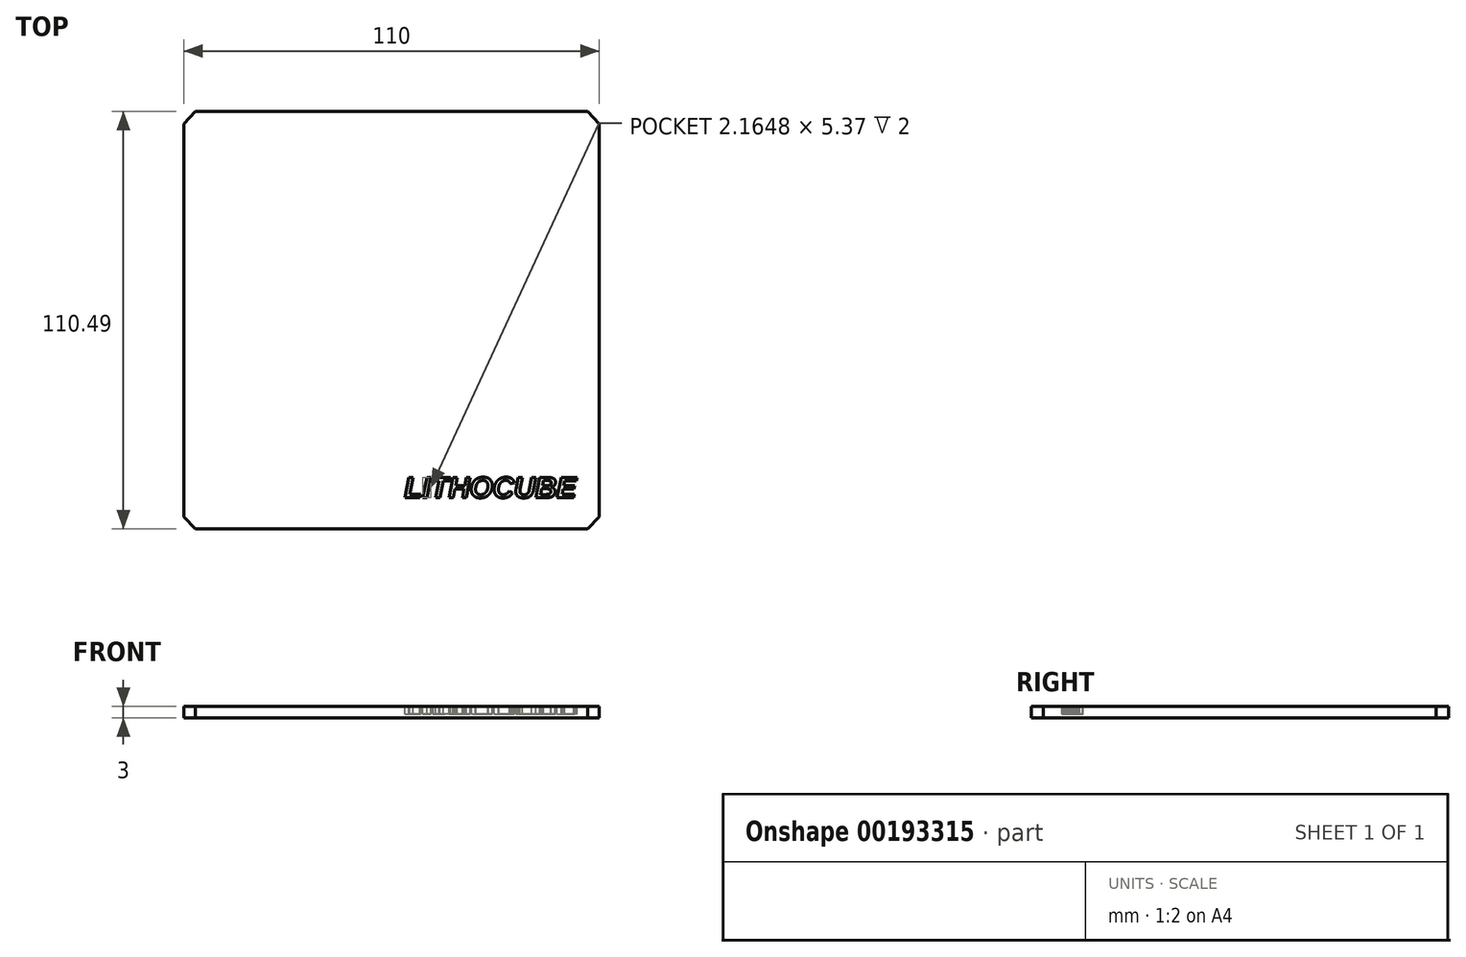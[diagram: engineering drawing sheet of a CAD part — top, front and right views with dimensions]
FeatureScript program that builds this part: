
annotation { "Feature Type Name" : "Feature", "Feature Type Description" : "" }
export const myFeature = defineFeature(function(context is Context, id is Id, definition is map)
    precondition{}
    {
        {
            var Q0;
            Q0=qCreatedBy(makeId("Top.planeOp"),FACE);
            var sketch = newSketch(context, id + "F0", { "sketchPlane" : qUnion([Q0])});
            skLineSegment(sketch, "E0", {"start": v(-66.37, -50.74) * mm, "end": v(-66.37, 53.26) * mm});
            skLineSegment(sketch, "E1", {"start": v(-66.37, 53.26) * mm, "end": v(-63.37, 56.5) * mm});
            skLineSegment(sketch, "E2", {"start": v(-63.37, 56.5) * mm, "end": v(40.63, 56.5) * mm});
            skLineSegment(sketch, "E3", {"start": v(40.63, 56.5) * mm, "end": v(43.63, 53.26) * mm});
            skLineSegment(sketch, "E4", {"start": v(43.63, 53.26) * mm, "end": v(43.63, -50.74) * mm});
            skLineSegment(sketch, "E5", {"start": v(43.63, -50.74) * mm, "end": v(40.63, -53.98) * mm});
            skLineSegment(sketch, "E6", {"start": v(40.63, -53.98) * mm, "end": v(-63.37, -53.98) * mm});
            skLineSegment(sketch, "E7", {"start": v(-63.37, -53.98) * mm, "end": v(-66.37, -50.74) * mm});
            skSolve(sketch);
        }
        {
            var Q0;
            Q0 = qSketchRegion(id + "F0", true);
            extrude(context, id + "F1", {"entities" : qUnion([Q0]), "depth" : 3 * mm});
        }
        {
            var Q0;
            {var subQ0=sQuery(id+"F0.wireOp",EDGE,"E1");var subQ1=sQuery(id+"F0.wireOp",EDGE,"E3");var subQ2=sQuery(id+"F0.wireOp",EDGE,"E0");var subQ3=sQuery(id+"F0.wireOp",EDGE,"E4");var subQ4=sQuery(id+"F0.wireOp",EDGE,"E5");var subQ5=sQuery(id+"F0.wireOp",EDGE,"E6");var subQ6=sQuery(id+"F0.wireOp",EDGE,"E7");var subQ7=sQuery(id+"F0.wireOp",EDGE,"E2");Q0=makeQuery(id+"F34qD7fa2nZmvgN_1.boolean.opBoolean","SPLIT",FACE,{"disambiguationData":[TD([makeQuery(id+"F1.opExtrude","SWEPT_FACE",FACE,{"disambiguationData":[OSD([subQ2])]})])],"derivedFrom":makeQuery(id+"F1.opExtrude","CAP_FACE",FACE,{"disambiguationData":[OSD([subQ2,subQ0,subQ7,subQ1,subQ3,subQ4,subQ5,subQ6])],"isStart":false})});}
            var sketch = newSketch(context, id + "F2", { "sketchPlane" : qUnion([Q0])});
            skSolve(sketch);
        }
        {
            var Q0;
            Q0=makeQuery(id+"F2.imprint","IMPRINT",FACE,{"disambiguationData":[TD([[makeQuery(id+"F2.imprint","IMPRINT",EDGE,{"derivedFrom":makeQuery(id+"F1.opExtrude","CAP_EDGE",EDGE,{"disambiguationData":[OSD([sQuery(id+"F0.wireOp",EDGE,"E0")])],"isStart":false})}),-1.0]])]});
            var sketch = newSketch(context, id + "F3", { "sketchPlane" : qUnion([Q0])});
            skText(sketch, "E8", { "text": "LITHOCUBE", "fontName": "Arimo-BoldItalic.ttf"});
            const initialGuessF3  = {"E8": [-0.00798, -0.04573, 1, 0, 0.00562]};
            skSetInitialGuess(sketch, initialGuessF3);
            skSolve(sketch);
        }
        {
            var Q0;
            Q0 = qSketchRegion(id + "F3", true);
            extrude(context, id + "F4", {"entities" : qUnion([Q0]), "operationType" : NewBodyOperationType.REMOVE, "oppositeDirection" : true, "depth" : 2 * mm});
        }
    });
